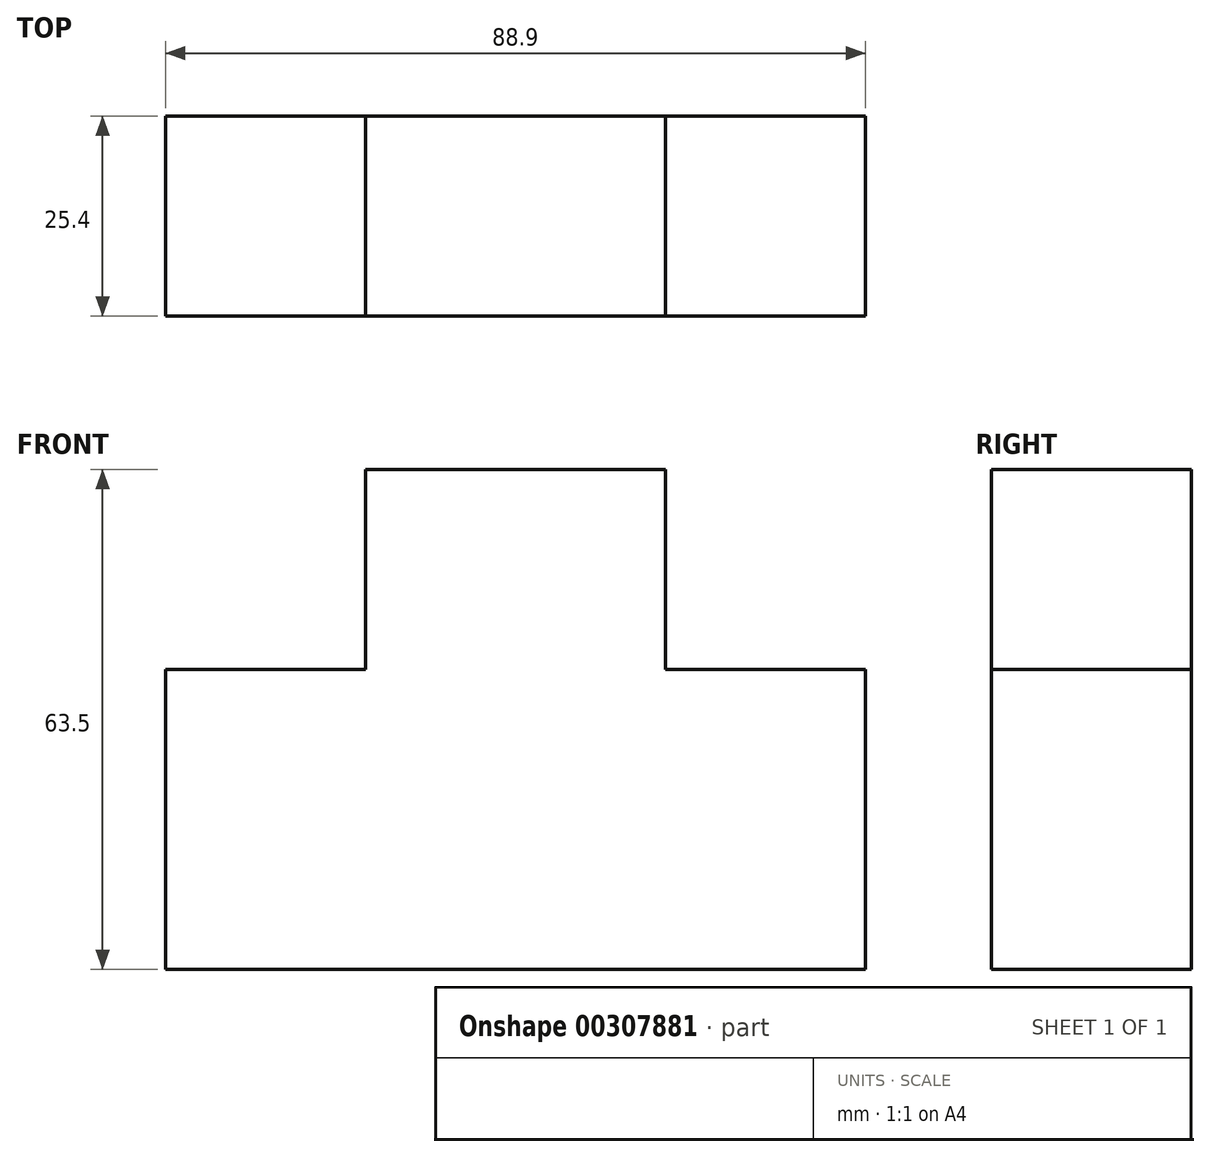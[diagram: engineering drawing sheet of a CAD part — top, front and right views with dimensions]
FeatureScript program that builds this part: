
annotation { "Feature Type Name" : "Feature", "Feature Type Description" : "" }
export const myFeature = defineFeature(function(context is Context, id is Id, definition is map)
    precondition{}
    {
        {
            var Q0;
            Q0=qCreatedBy(makeId("Front.planeOp"),FACE);
            var sketch = newSketch(context, id + "F0", { "sketchPlane" : qUnion([Q0])});
            skLineSegment(sketch, "E0", {"start": v(-42.6, -37.07) * mm, "end": v(46.3, -37.07) * mm});
            skLineSegment(sketch, "E1", {"start": v(46.3, -37.07) * mm, "end": v(46.3, 1.03) * mm});
            skLineSegment(sketch, "E2", {"start": v(46.3, 1.03) * mm, "end": v(20.9, 1.03) * mm});
            skLineSegment(sketch, "E3", {"start": v(20.9, 1.03) * mm, "end": v(20.9, 26.43) * mm});
            skLineSegment(sketch, "E4", {"start": v(20.9, 26.43) * mm, "end": v(-17.2, 26.43) * mm});
            skLineSegment(sketch, "E5", {"start": v(-17.2, 26.43) * mm, "end": v(-17.2, 1.03) * mm});
            skLineSegment(sketch, "E6", {"start": v(-17.2, 1.03) * mm, "end": v(-42.6, 1.03) * mm});
            skLineSegment(sketch, "E7", {"start": v(-42.6, 1.03) * mm, "end": v(-42.6, -37.07) * mm});
            skSolve(sketch);
        }
        {
            var Q0;
            Q0=makeQuery(id+"F0.imprint","IMPRINT",FACE,{"disambiguationData":[TD([[makeQuery(id+"F0.imprint","IMPRINT",EDGE,{"derivedFrom":sQuery(id+"F0.wireOp",EDGE,"E0")}),1.0]])]});
            extrude(context, id + "F1", {"entities" : qUnion([Q0]), "depth" : 25.4 * mm});
        }
    });
